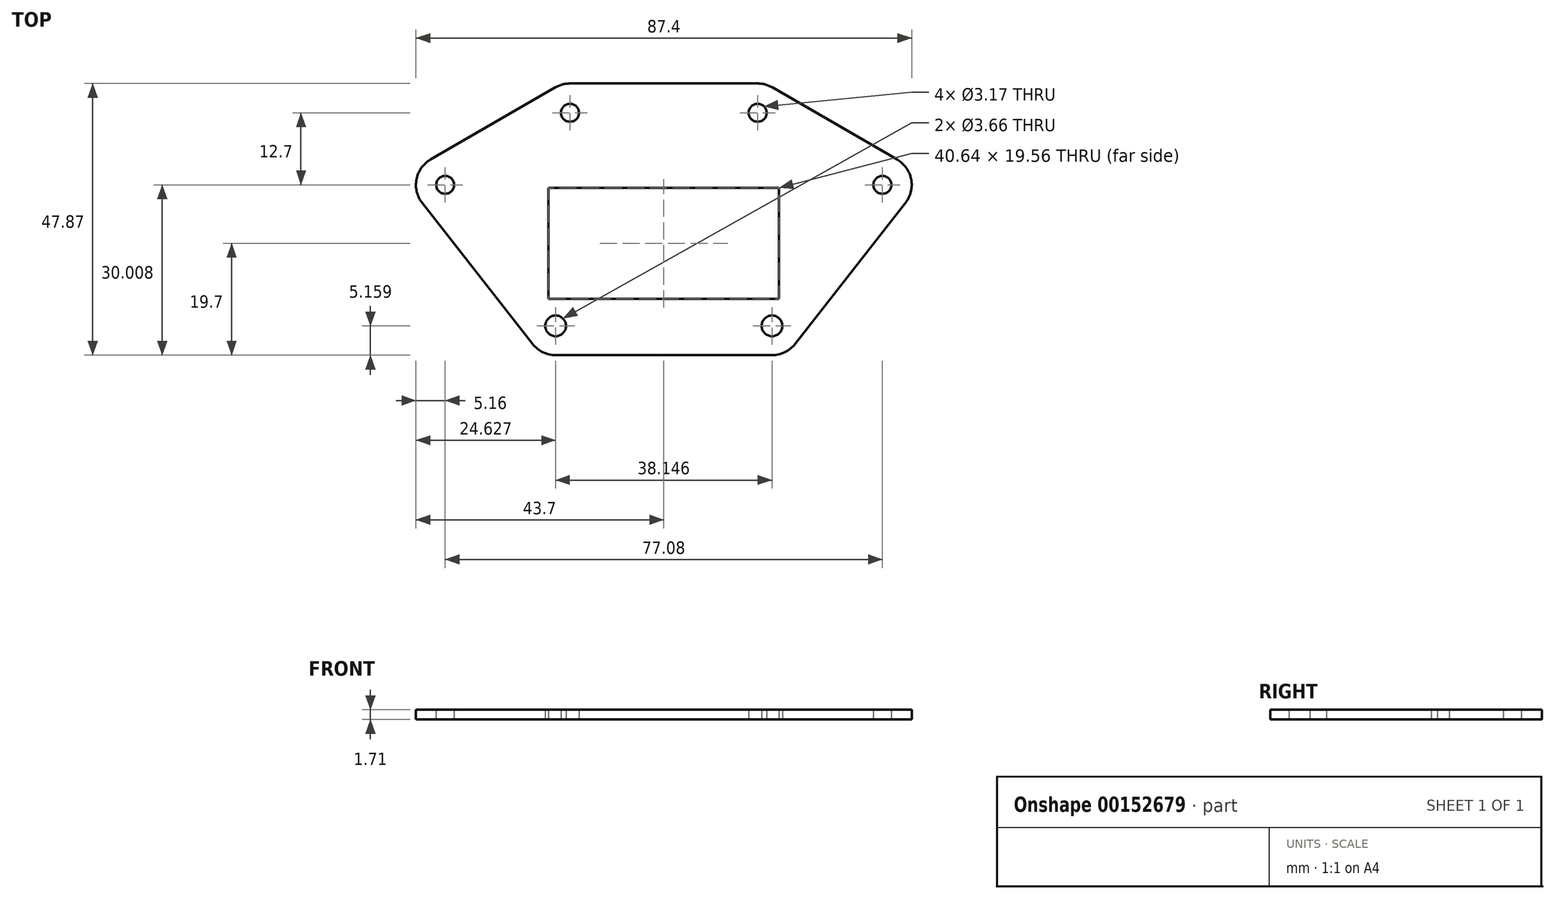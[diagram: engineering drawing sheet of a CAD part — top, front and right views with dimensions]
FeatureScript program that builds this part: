
annotation { "Feature Type Name" : "Feature", "Feature Type Description" : "" }
export const myFeature = defineFeature(function(context is Context, id is Id, definition is map)
    precondition{}
    {
        {
            var Q0;
            Q0=qCreatedBy(makeId("Top.planeOp"),FACE);
            var sketch = newSketch(context, id + "F0", { "sketchPlane" : qUnion([Q0])});
            skLineSegment(sketch, "E0.top", {"start": v(20.32, -9.78) * mm, "end": v(-20.32, -9.78) * mm});
            skLineSegment(sketch, "E1.top", {"start": v(20.32, 9.78) * mm, "end": v(-20.32, 9.78) * mm});
            skLineSegment(sketch, "E2", {"start": v(0, -9.78) * mm, "end": v(0, 9.78) * mm, "construction": true});
            skPoint(sketch, "E3.middle", {"position": v(0, 0) * mm});
            skLineSegment(sketch, "E4", {"start": v(0, 9.78) * mm, "end": v(0, 23) * mm, "construction": true});
            skLineSegment(sketch, "E5", {"start": v(-16.54, 23) * mm, "end": v(16.54, 23) * mm, "construction": true});
            skLineSegment(sketch, "E6", {"start": v(16.54, 23) * mm, "end": v(38.54, 10.3) * mm, "construction": true});
            skLineSegment(sketch, "E7", {"start": v(-16.54, 23) * mm, "end": v(-38.54, 10.3) * mm, "construction": true});
            skCircle(sketch, "E8", {"center": v(38.54, 10.3) * mm, "radius": 1.59 * mm});
            skCircle(sketch, "E9", {"center": v(16.54, 23) * mm, "radius": 1.59 * mm});
            skCircle(sketch, "E10", {"center": v(-16.54, 23) * mm, "radius": 1.59 * mm});
            skCircle(sketch, "E11", {"center": v(-38.54, 10.3) * mm, "radius": 1.59 * mm});
            skLineSegment(sketch, "E12", {"start": v(0, 23) * mm, "end": v(0, 28.17) * mm, "construction": true});
            skLineSegment(sketch, "E13", {"start": v(38.54, 10.3) * mm, "end": v(0, 10.3) * mm, "construction": true});
            skLineSegment(sketch, "E14", {"start": v(0, 10.3) * mm, "end": v(-38.54, 10.3) * mm, "construction": true});
            skLineSegment(sketch, "E15", {"start": v(-16.54, 28.17) * mm, "end": v(16.54, 28.17) * mm});
            skArc(sketch, "E16", {"start": v(42.6, 7.13) * mm, "mid": v(43.6, 11.29) * mm, "end": v(41.12, 14.78) * mm});
            skArc(sketch, "E17", {"start": v(19.12, 27.48) * mm, "mid": v(17.88, 28) * mm, "end": v(16.54, 28.17) * mm});
            skArc(sketch, "E18", {"start": v(-16.54, 28.17) * mm, "mid": v(-17.88, 28) * mm, "end": v(-19.12, 27.48) * mm});
            skArc(sketch, "E19", {"start": v(-41.12, 14.78) * mm, "mid": v(-43.6, 11.29) * mm, "end": v(-42.6, 7.13) * mm});
            skLineSegment(sketch, "E20", {"start": v(19.12, 27.48) * mm, "end": v(41.12, 14.78) * mm});
            skLineSegment(sketch, "E21", {"start": v(-19.12, 27.48) * mm, "end": v(-41.12, 14.78) * mm});
            skLineSegment(sketch, "E22", {"start": v(-42.6, 7.13) * mm, "end": v(-23.13, -17.72) * mm});
            skLineSegment(sketch, "E23", {"start": v(42.6, 7.13) * mm, "end": v(23.13, -17.72) * mm});
            skArc(sketch, "E24", {"start": v(-23.13, -17.72) * mm, "mid": v(-21.33, -19.18) * mm, "end": v(-19.07, -19.7) * mm});
            skArc(sketch, "E25", {"start": v(19.07, -19.7) * mm, "mid": v(21.33, -19.18) * mm, "end": v(23.13, -17.72) * mm});
            skLineSegment(sketch, "E26", {"start": v(0, -9.78) * mm, "end": v(0, -14.54) * mm, "construction": true});
            skLineSegment(sketch, "E27", {"start": v(-19.07, -14.54) * mm, "end": v(19.07, -14.54) * mm, "construction": true});
            skLineSegment(sketch, "E28", {"start": v(0, -14.54) * mm, "end": v(0, -19.7) * mm, "construction": true});
            skLineSegment(sketch, "E29", {"start": v(-19.07, -19.7) * mm, "end": v(19.07, -19.7) * mm});
            skCircle(sketch, "E30", {"center": v(-19.07, -14.54) * mm, "radius": 1.83 * mm});
            skCircle(sketch, "E31", {"center": v(19.07, -14.54) * mm, "radius": 1.83 * mm});
            skLineSegment(sketch, "E32", {"start": v(-20.32, -9.78) * mm, "end": v(-20.32, 9.78) * mm});
            skLineSegment(sketch, "E33", {"start": v(20.32, -9.78) * mm, "end": v(20.32, 9.78) * mm});
            skLineSegment(sketch, "E34", {"start": v(-20.32, 0) * mm, "end": v(-10.9, 0) * mm, "construction": true});
            skLineSegment(sketch, "E35", {"start": v(-10.9, 0) * mm, "end": v(-16.54, 23) * mm, "construction": true});
            skLineSegment(sketch, "E36.bottom", {"start": v(24.9, 4.89) * mm, "end": v(-24.9, 4.89) * mm, "construction": true});
            skLineSegment(sketch, "E36.top", {"start": v(24.9, -4.89) * mm, "end": v(-24.9, -4.89) * mm, "construction": true});
            skLineSegment(sketch, "E36.left", {"start": v(24.9, 4.89) * mm, "end": v(24.9, -4.89) * mm, "construction": true});
            skLineSegment(sketch, "E36.right", {"start": v(-24.9, 4.89) * mm, "end": v(-24.9, -4.89) * mm, "construction": true});
            skCircle(sketch, "E37", {"center": v(24.9, 4.89) * mm, "radius": 2.3 * mm, "construction": true});
            skCircle(sketch, "E38", {"center": v(24.9, -4.89) * mm, "radius": 3.32 * mm, "construction": true});
            skLineSegment(sketch, "E39", {"start": v(24.9, -4.89) * mm, "end": v(33.85, 2.86) * mm, "construction": true});
            skSolve(sketch);
        }
        {
            var Q0;
            Q0=qSketchRegion(id+"F0",true);
            extrude(context, id + "F1", {"entities" : qUnion([Q0]), "depth" : 1.7 * mm});
        }
    });
